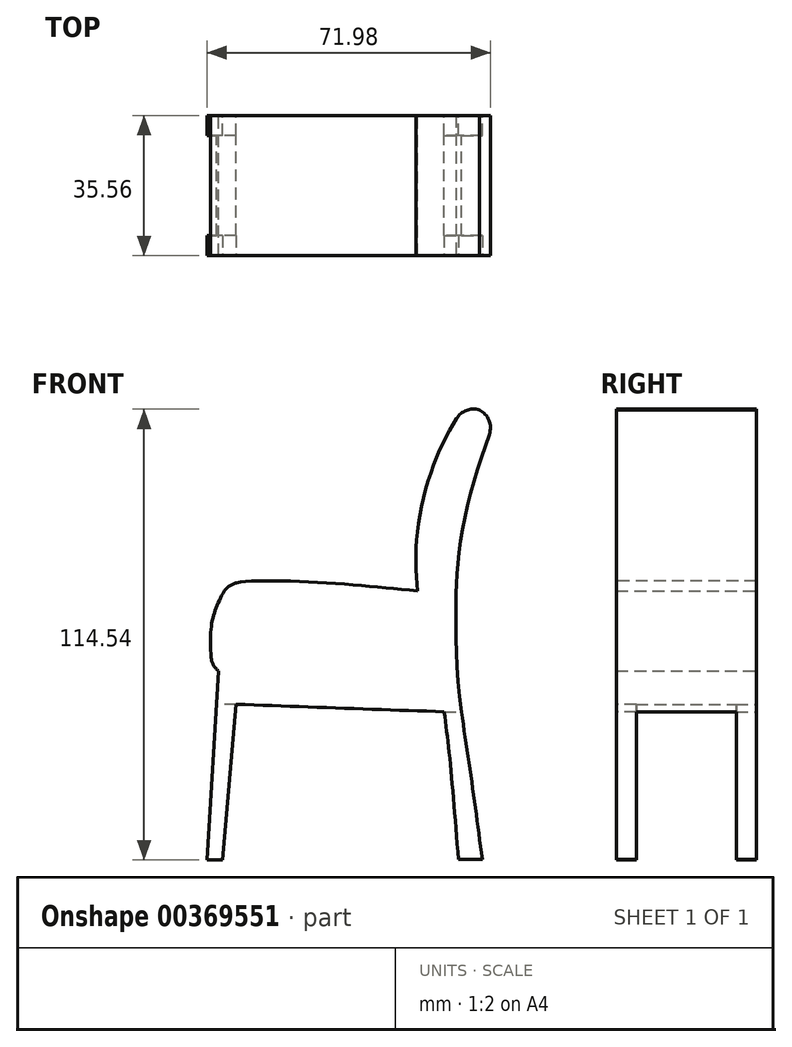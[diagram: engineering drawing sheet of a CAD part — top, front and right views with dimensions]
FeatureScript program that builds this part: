
annotation { "Feature Type Name" : "Feature", "Feature Type Description" : "" }
export const myFeature = defineFeature(function(context is Context, id is Id, definition is map)
    precondition{}
    {
        {
            var Q0;
            Q0=qCreatedBy(makeId("Front.planeOp"),FACE);
            var sketch = newSketch(context, id + "F0", { "sketchPlane" : qUnion([Q0])});
            skFitSpline(sketch, "E0", {"points": [v(-37.04, 14.08) * mm, v(-32.73, 15.07) * mm, v(-11.2, 14.74) * mm, v(11.33, 12.76) * mm], "startDerivative": vector(18.53, 6.33) * mm, "endDerivative": vector(51.95, -5.31) * mm});
            skFitSpline(sketch, "E1", {"points": [v(11.33, 12.76) * mm, v(11.33, 27.66) * mm, v(16.3, 46.88) * mm, v(22.93, 59.14) * mm], "startDerivative": vector(-2.82, 44.32) * mm, "endDerivative": vector(22.46, 36.16) * mm});
            skFitSpline(sketch, "E2", {"points": [v(22.93, 59.14) * mm, v(26.03, 59.14) * mm, v(31.04, 56.6) * mm], "startDerivative": vector(6.95, 0.94) * mm, "endDerivative": vector(9.16, -5.68) * mm});
            skFitSpline(sketch, "E3", {"points": [v(31.04, 56.6) * mm, v(26.44, 42.96) * mm, v(22.93, 29.03) * mm, v(21.43, 17.05) * mm, v(21.15, 7.85) * mm, v(21.53, -8.61) * mm, v(24.52, -31.3) * mm, v(27.83, -55.5) * mm], "startDerivative": vector(-35.04, -99.57) * mm, "endDerivative": vector(17.97, -136.84) * mm});
            skFitSpline(sketch, "E4", {"points": [v(27.83, -55.5) * mm, v(21.76, -55.5) * mm], "startDerivative": vector(-6.07, 0) * mm, "endDerivative": vector(-6.07, 0) * mm});
            skFitSpline(sketch, "E5", {"points": [v(21.76, -55.5) * mm, v(19.67, -30.77) * mm, v(18.14, -17.96) * mm], "startDerivative": vector(-3.58, 46.03) * mm, "endDerivative": vector(-3.67, 28.08) * mm});
            skFitSpline(sketch, "E6", {"points": [v(18.14, -17.96) * mm, v(-34.7, -16.07) * mm], "startDerivative": vector(-51.4, 1.81) * mm, "endDerivative": vector(-51.4, 1.81) * mm});
            skFitSpline(sketch, "E7", {"points": [v(-34.7, -16.07) * mm, v(-38.18, -55.6) * mm], "startDerivative": vector(-3.48, -39.52) * mm, "endDerivative": vector(-3.48, -39.52) * mm});
            skFitSpline(sketch, "E8", {"points": [v(-38.18, -55.6) * mm, v(-42.08, -55.6) * mm], "startDerivative": vector(-3.9, 0) * mm, "endDerivative": vector(-3.9, 0) * mm});
            skFitSpline(sketch, "E9", {"points": [v(-42.08, -55.6) * mm, v(-39.21, -7.59) * mm], "startDerivative": vector(2.87, 48) * mm, "endDerivative": vector(2.87, 48) * mm});
            skFitSpline(sketch, "E10", {"points": [v(-39.21, -7.59) * mm, v(-40.78, -7.59) * mm], "startDerivative": vector(-1.57, 0) * mm, "endDerivative": vector(-1.57, 0) * mm});
            skFitSpline(sketch, "E11", {"points": [v(-40.78, -7.59) * mm, v(-40.78, 5.03) * mm, v(-37.04, 14.08) * mm], "startDerivative": vector(-2.12, 24.9) * mm, "endDerivative": vector(9.87, 18.29) * mm});
            skLineSegment(sketch, "E12", {"start": v(-34.7, -16.07) * mm, "end": v(-39.72, -16.07) * mm});
            skLineSegment(sketch, "E13", {"start": v(18.14, -17.96) * mm, "end": v(22.55, -17.96) * mm});
            skSolve(sketch);
        }
        {
            var Q0;
            Q0=makeQuery(id+"F0.imprint","IMPRINT",FACE,{"disambiguationData":[TD([[makeQuery(id+"F0.imprint","IMPRINT",EDGE,{"derivedFrom":sQuery(id+"F0.wireOp",EDGE,"E0")}),-1.0]])]});
            extrude(context, id + "F1", {"entities" : qUnion([Q0]), "depth" : 17.78 * mm});
        }
        {
            var Q0;
            Q0=makeQuery(id+"F0.imprint","IMPRINT",FACE,{"disambiguationData":[TD([[makeQuery(id+"F0.imprint","IMPRINT",EDGE,{"derivedFrom":sQuery(id+"F0.wireOp",EDGE,"E7")}),-1.0]])]});
            var Q1;
            {var subQ0=sQuery(id+"F0.wireOp",EDGE,"E4");Q1=makeQuery(id+"F0.imprint","IMPRINT",FACE,{"disambiguationData":[TD([[makeQuery(id+"F0.imprint","IMPRINT",EDGE,{"derivedFrom":subQ0}),-1.0]])]});}
            extrude(context, id + "F2", {"entities" : qUnion([Q0, Q1]), "operationType" : NewBodyOperationType.ADD, "depth" : 5.08 * mm});
        }
        {
            var Q0;
            Q0=makeQuery(id+"F1.opExtrude","SWEPT_EDGE",EDGE,{"disambiguationData":[OSD([sQuery(id+"F0.wireOp",EDGE,"E10"),sQuery(id+"F0.wireOp",EDGE,"E11")])]});
            var Q1;
            Q1=makeQuery(id+"F1.opExtrude","SWEPT_EDGE",EDGE,{"disambiguationData":[OSD([sQuery(id+"F0.wireOp",EDGE,"E0"),sQuery(id+"F0.wireOp",EDGE,"E11")])]});
            var Q2;
            Q2=makeQuery(id+"F1.opExtrude","SWEPT_EDGE",EDGE,{"disambiguationData":[OSD([sQuery(id+"F0.wireOp",EDGE,"E1"),sQuery(id+"F0.wireOp",EDGE,"E2")])]});
            var Q3;
            Q3=makeQuery(id+"F1.opExtrude","SWEPT_EDGE",EDGE,{"disambiguationData":[OSD([sQuery(id+"F0.wireOp",EDGE,"E2"),sQuery(id+"F0.wireOp",EDGE,"E3")])]});
            fillet(context, id + "F3", {"entities" : qUnion([Q0, Q1, Q2, Q3]), "radius" : 5.08 * mm, "tangentPropagation" : true, "allowEdgeOverflow" : false});
        }
        {
            var Q0;
            Q0=makeQuery(id+"F1.opExtrude","CAP_FACE",FACE,{"disambiguationData":[OSD([sQuery(id+"F0.wireOp",EDGE,"E0"),sQuery(id+"F0.wireOp",EDGE,"E1"),sQuery(id+"F0.wireOp",EDGE,"E2"),sQuery(id+"F0.wireOp",EDGE,"E3"),sQuery(id+"F0.wireOp",EDGE,"E6"),sQuery(id+"F0.wireOp",EDGE,"E9"),sQuery(id+"F0.wireOp",EDGE,"E10"),sQuery(id+"F0.wireOp",EDGE,"E11"),sQuery(id+"F0.wireOp",EDGE,"E12"),sQuery(id+"F0.wireOp",EDGE,"E13")])],"isStart":false});
            cPlane(context, id + "F4", {"entities" : qUnion([Q0]), "cplaneType" : CPlaneType.OFFSET, "offset" : 0 * mm, "width" : 152.4 * mm, "height" : 152.4 * mm});
        }
        {
            var Q0;
            Q0=makeQuery(id+"F1.opExtrude","SWEPT_BODY",BODY,{"disambiguationData":[OSD([sQuery(id+"F0.wireOp",EDGE,"E0"),sQuery(id+"F0.wireOp",EDGE,"E1"),sQuery(id+"F0.wireOp",EDGE,"E2"),sQuery(id+"F0.wireOp",EDGE,"E3"),sQuery(id+"F0.wireOp",EDGE,"E6"),sQuery(id+"F0.wireOp",EDGE,"E9"),sQuery(id+"F0.wireOp",EDGE,"E10"),sQuery(id+"F0.wireOp",EDGE,"E11"),sQuery(id+"F0.wireOp",EDGE,"E12"),sQuery(id+"F0.wireOp",EDGE,"E13")])]});
            var Q1;
            Q1=qCreatedBy(id+"F4.planeOp",FACE);
            mirror(context, id + "F5", {"operationType" : NewBodyOperationType.ADD, "entities" : qUnion([Q0]), "mirrorPlane" : qUnion([Q1])});
        }
    });
